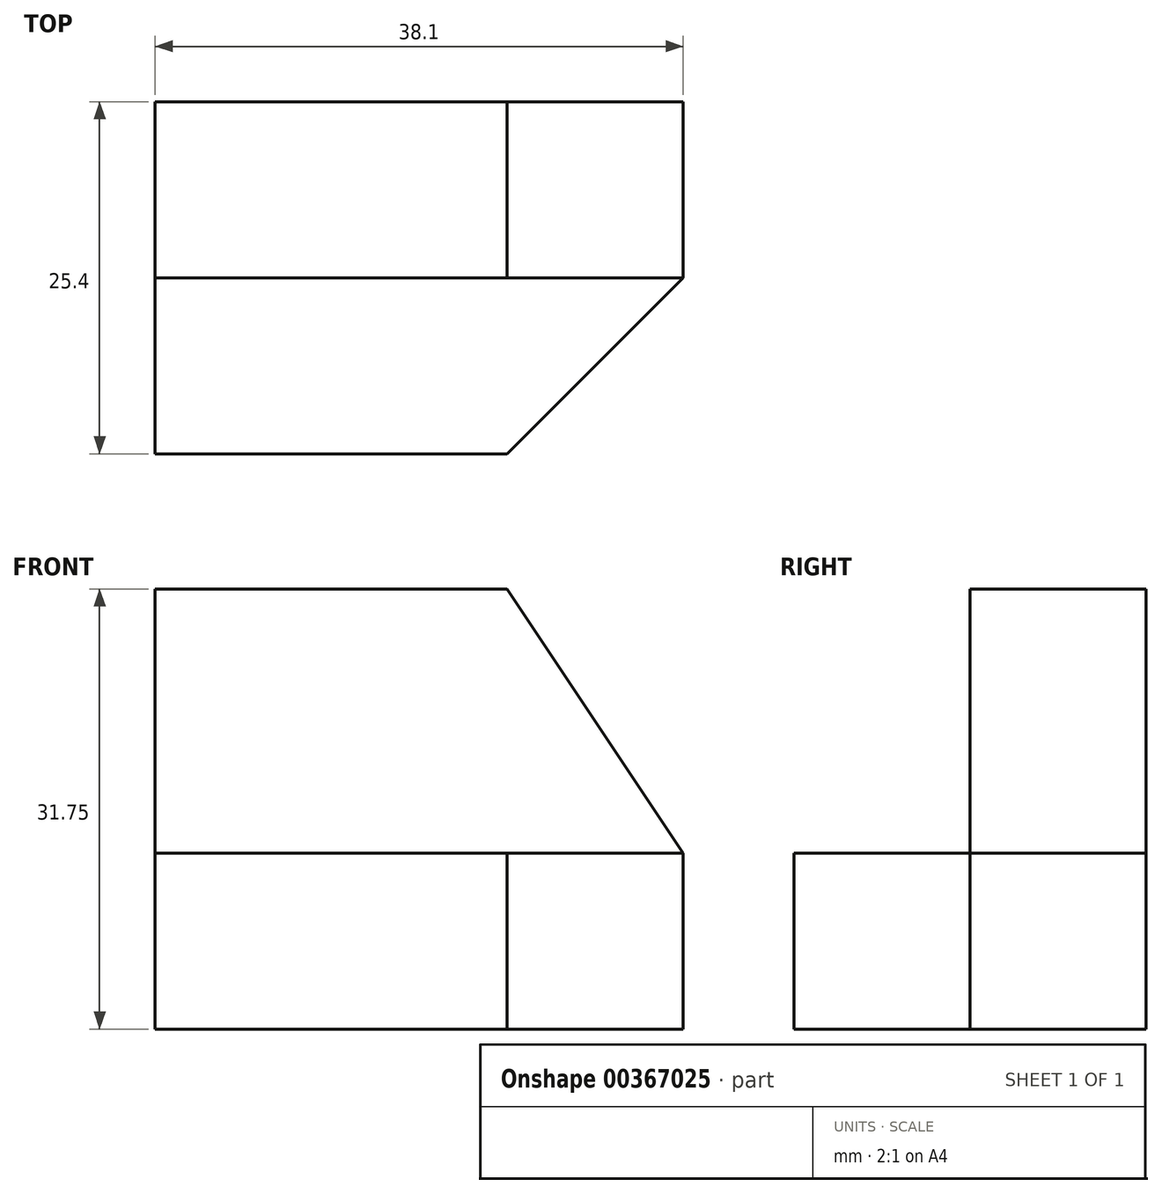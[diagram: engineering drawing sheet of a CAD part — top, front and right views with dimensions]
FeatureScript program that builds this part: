
annotation { "Feature Type Name" : "Feature", "Feature Type Description" : "" }
export const myFeature = defineFeature(function(context is Context, id is Id, definition is map)
    precondition{}
    {
        {
            var Q0;
            Q0=qCreatedBy(makeId("Right.planeOp"),FACE);
            var sketch = newSketch(context, id + "F0", { "sketchPlane" : qUnion([Q0])});
            skLineSegment(sketch, "E0", {"start": v(0, 0) * mm, "end": v(25.4, 0) * mm});
            skLineSegment(sketch, "E1", {"start": v(25.4, 0) * mm, "end": v(25.4, 31.75) * mm});
            skLineSegment(sketch, "E2", {"start": v(25.4, 31.75) * mm, "end": v(12.7, 31.75) * mm});
            skLineSegment(sketch, "E3", {"start": v(12.7, 31.75) * mm, "end": v(12.7, 12.7) * mm});
            skLineSegment(sketch, "E4", {"start": v(12.7, 12.7) * mm, "end": v(0, 12.7) * mm});
            skLineSegment(sketch, "E5", {"start": v(0, 12.7) * mm, "end": v(0, 0) * mm});
            skSolve(sketch);
        }
        {
            var Q0;
            Q0 = qSketchRegion(id + "F0", true);
            extrude(context, id + "F1", {"entities" : qUnion([Q0]), "depth" : 38.1 * mm});
        }
        {
            var Q0;
            Q0=makeQuery(id+"F1.opExtrude","SWEPT_FACE",FACE,{"disambiguationData":[OSD([sQuery(id+"F0.wireOp",EDGE,"E3")])]});
            var sketch = newSketch(context, id + "F2", { "sketchPlane" : qUnion([Q0])});
            skLineSegment(sketch, "E6", {"start": v(38.1, 12.7) * mm, "end": v(25.4, 31.75) * mm});
            skSolve(sketch);
        }
        {
            var Q0;
            Q0 = qSketchRegion(id + "F2", true);
            var Q1;
            {var subQ0=sQuery(id+"F2.wireOp",EDGE,"E6");Q1=makeQuery(id+"F2.imprint","IMPRINT",FACE,{"disambiguationData":[TD([[makeQuery(id+"F2.imprint","IMPRINT",EDGE,{"derivedFrom":subQ0}),-1.0]])]});}
            extrude(context, id + "F3", {"entities" : qUnion([Q0, Q1]), "operationType" : NewBodyOperationType.REMOVE, "oppositeDirection" : true, "depth" : 12.7 * mm});
        }
        {
            var Q0;
            Q0=makeQuery(id+"F1.opExtrude","SWEPT_FACE",FACE,{"disambiguationData":[OSD([sQuery(id+"F0.wireOp",EDGE,"E4")])]});
            var sketch = newSketch(context, id + "F4", { "sketchPlane" : qUnion([Q0])});
            skLineSegment(sketch, "E7", {"start": v(38.1, 12.7) * mm, "end": v(25.4, 0) * mm});
            skSolve(sketch);
        }
        {
            var Q0;
            Q0 = qSketchRegion(id + "F4", true);
            var Q1;
            {var subQ0=sQuery(id+"F4.wireOp",EDGE,"E7");Q1=makeQuery(id+"F4.imprint","IMPRINT",FACE,{"disambiguationData":[TD([[makeQuery(id+"F4.imprint","IMPRINT",EDGE,{"derivedFrom":subQ0}),1.0]])]});}
            extrude(context, id + "F5", {"entities" : qUnion([Q0, Q1]), "operationType" : NewBodyOperationType.REMOVE, "oppositeDirection" : true, "depth" : 12.7 * mm});
        }
    });
